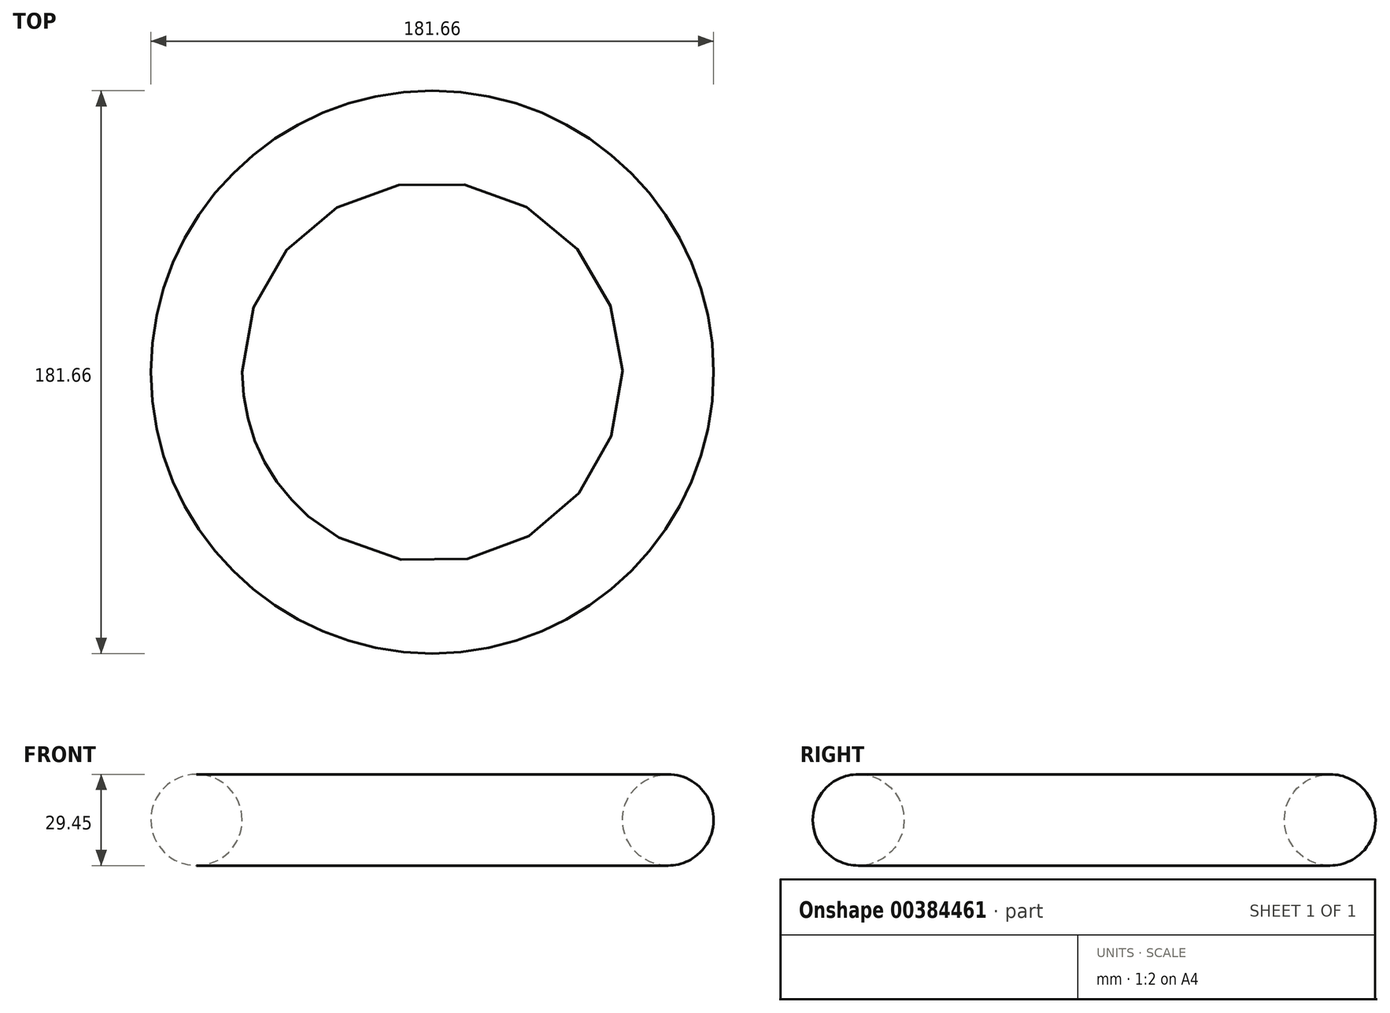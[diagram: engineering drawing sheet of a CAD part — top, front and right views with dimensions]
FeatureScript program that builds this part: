
annotation { "Feature Type Name" : "Feature", "Feature Type Description" : "" }
export const myFeature = defineFeature(function(context is Context, id is Id, definition is map)
    precondition{}
    {
        {
            var Q0;
            Q0=qCreatedBy(makeId("Front.planeOp"),FACE);
            var sketch = newSketch(context, id + "F0", { "sketchPlane" : qUnion([Q0])});
            skLineSegment(sketch, "E0", {"start": v(0, 0) * mm, "end": v(0, 96.33) * mm, "construction": true});
            skCircle(sketch, "E1", {"center": v(76.1, 9.32) * mm, "radius": 14.72 * mm});
            skSolve(sketch);
        }
        {
            var Q0;
            Q0=makeQuery(id+"F0.imprint","IMPRINT",FACE,{"disambiguationData":[TD([[makeQuery(id+"F0.imprint","IMPRINT",EDGE,{"derivedFrom":sQuery(id+"F0.wireOp",EDGE,"E1")}),1.0]])]});
            var Q1;
            Q1=sQuery(id+"F0.wireOp",EDGE,"E0");
            revolve(context, id + "F1", {"entities" : qUnion([Q0]), "axis" : qUnion([Q1]), "revolveType" : RevolveType.FULL});
        }
    });
